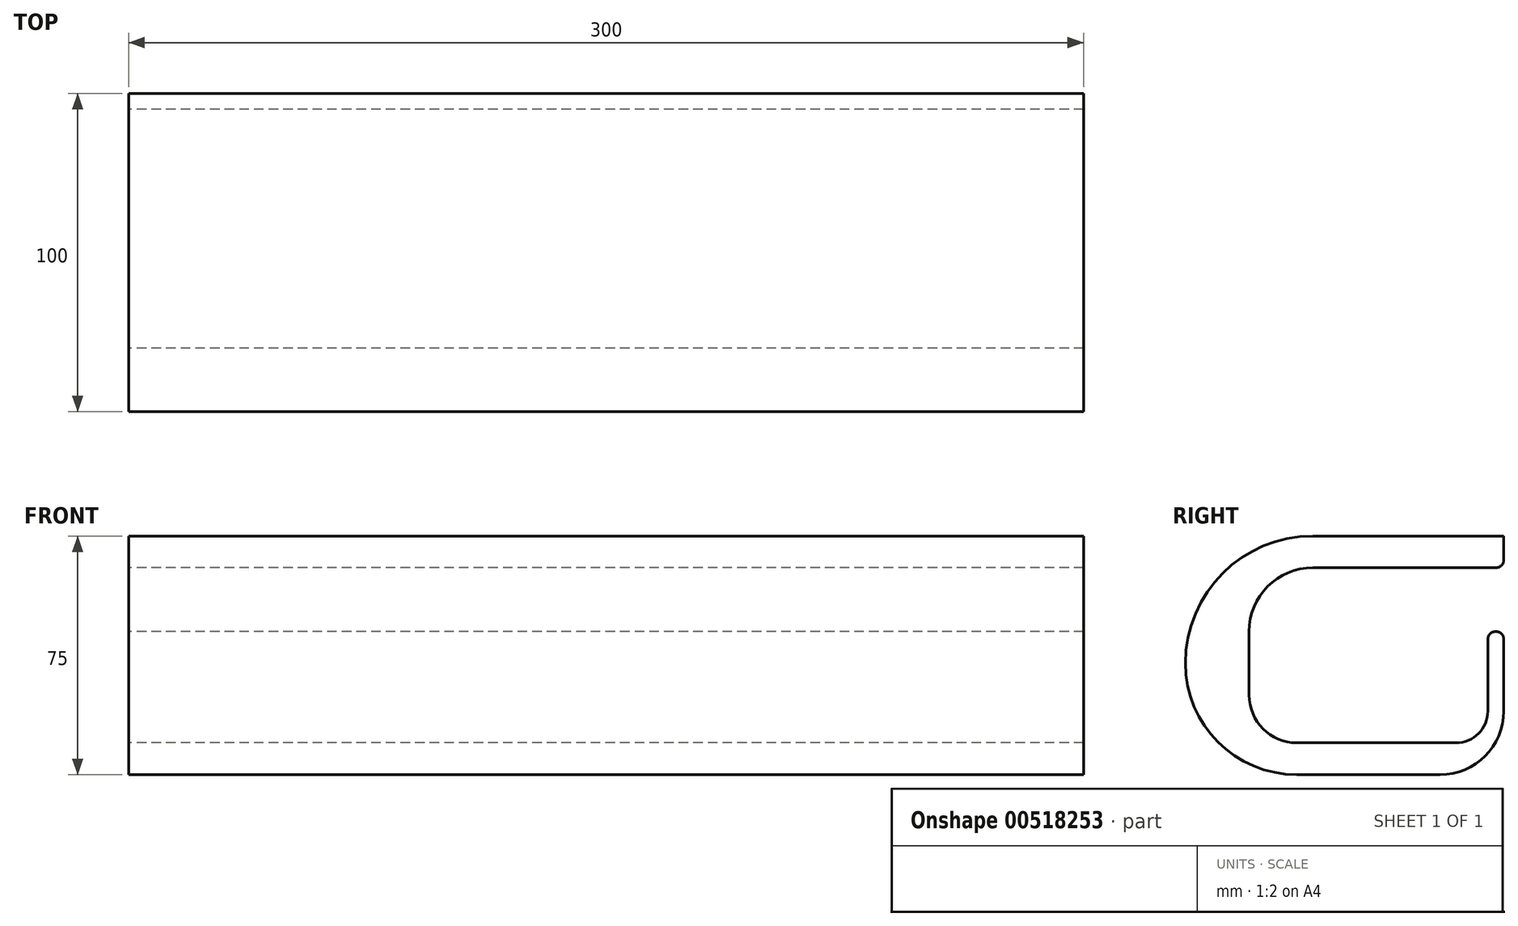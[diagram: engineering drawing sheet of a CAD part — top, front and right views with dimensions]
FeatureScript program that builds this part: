
annotation { "Feature Type Name" : "Feature", "Feature Type Description" : "" }
export const myFeature = defineFeature(function(context is Context, id is Id, definition is map)
    precondition{}
    {
        {
            var Q0;
            Q0=qCreatedBy(makeId("Right.planeOp"),FACE);
            var sketch = newSketch(context, id + "F0", { "sketchPlane" : qUnion([Q0])});
            skLineSegment(sketch, "E0", {"start": v(0, 0) * mm, "end": v(0, -10) * mm});
            skLineSegment(sketch, "E1", {"start": v(0, 0) * mm, "end": v(-60, 0) * mm});
            skLineSegment(sketch, "E2", {"start": v(-100, -40) * mm, "end": v(-100, -40) * mm});
            skLineSegment(sketch, "E3", {"start": v(-65, -75) * mm, "end": v(-20, -75) * mm});
            skLineSegment(sketch, "E4", {"start": v(0, -10) * mm, "end": v(-60, -10) * mm});
            skLineSegment(sketch, "E5", {"start": v(-80, -30) * mm, "end": v(-80, -50) * mm});
            skLineSegment(sketch, "E6", {"start": v(-65, -65) * mm, "end": v(-15, -65) * mm});
            skLineSegment(sketch, "E7", {"start": v(-5, -55) * mm, "end": v(-5, -30) * mm});
            skLineSegment(sketch, "E8", {"start": v(-5, -30) * mm, "end": v(0, -30) * mm});
            skLineSegment(sketch, "E9", {"start": v(0, -30) * mm, "end": v(0, -55) * mm});
            skPoint(sketch, "E10.visualSharp", {"position": v(-80, -10) * mm});
            skArc(sketch, "E10.filletArc", {"start": v(-60, -10) * mm, "mid": v(-74.14, -15.86) * mm, "end": v(-80, -30) * mm});
            skPoint(sketch, "E11.visualSharp", {"position": v(-80, -65) * mm});
            skArc(sketch, "E11.filletArc", {"start": v(-80, -50) * mm, "mid": v(-75.6, -60.6) * mm, "end": v(-65, -65) * mm});
            skPoint(sketch, "E12.visualSharp", {"position": v(-5, -65) * mm});
            skArc(sketch, "E12.filletArc", {"start": v(-15, -65) * mm, "mid": v(-7.93, -62.07) * mm, "end": v(-5, -55) * mm});
            skPoint(sketch, "E13.visualSharp", {"position": v(0, -75) * mm});
            skArc(sketch, "E13.filletArc", {"start": v(-20, -75) * mm, "mid": v(-5.86, -69.14) * mm, "end": v(0, -55) * mm});
            skPoint(sketch, "E14.visualSharp", {"position": v(-100, -75) * mm});
            skArc(sketch, "E14.filletArc", {"start": v(-100, -40) * mm, "mid": v(-89.75, -64.75) * mm, "end": v(-65, -75) * mm});
            skPoint(sketch, "E15.visualSharp", {"position": v(-100, 0) * mm});
            skArc(sketch, "E15.filletArc", {"start": v(-60, 0) * mm, "mid": v(-88.28, -11.72) * mm, "end": v(-100, -40) * mm});
            skSolve(sketch);
        }
        {
            var Q0;
            Q0=makeQuery(id+"F0.imprint","IMPRINT",FACE,{"disambiguationData":[TD([[makeQuery(id+"F0.imprint","IMPRINT",EDGE,{"derivedFrom":sQuery(id+"F0.wireOp",EDGE,"E0")}),-1.0]])]});
            extrude(context, id + "F1", {"entities" : qUnion([Q0]), "depth" : 300 * mm, "offsetDistance" : 25 * mm});
        }
        {
            var Q0;
            Q0=makeQuery(id+"F1.opExtrude","SWEPT_EDGE",EDGE,{"disambiguationData":[OSD([sQuery(id+"F0.wireOp",EDGE,"E0"),sQuery(id+"F0.wireOp",EDGE,"E4")])]});
            var Q1;
            Q1=makeQuery(id+"F1.opExtrude","SWEPT_EDGE",EDGE,{"disambiguationData":[OSD([sQuery(id+"F0.wireOp",EDGE,"E8"),sQuery(id+"F0.wireOp",EDGE,"E9")])]});
            var Q2;
            Q2=makeQuery(id+"F1.opExtrude","SWEPT_EDGE",EDGE,{"disambiguationData":[OSD([sQuery(id+"F0.wireOp",EDGE,"E7"),sQuery(id+"F0.wireOp",EDGE,"E8")])]});
            fillet(context, id + "F2", {"entities" : qUnion([Q0, Q1, Q2]), "radius" : 2.5 * mm, "tangentPropagation" : true, "allowEdgeOverflow" : false});
        }
    });
